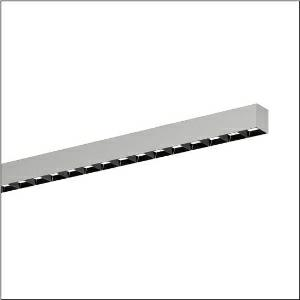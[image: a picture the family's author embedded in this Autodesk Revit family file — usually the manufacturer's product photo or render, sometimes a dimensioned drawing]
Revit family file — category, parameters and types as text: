
# Revit family: silica_21_51mx22tat4s
name_source: partatom
category: Lighting Fixtures
units: mm (PartAtom-declared; Revit-internal decimal feet)

## family parameters
Cut with Voids When Loaded = No
Host = Face
Light Source = No
Part Type = Normal
Room Calculation Point = No
Round Connector Dimension = Use Diameter
Shared = No

## types (1)
- --- (1 x LED, 3720 lm, 32.1 W, 6500K)
    Apparent Load = 32 VA
    CIE Flux Codes = 84 100 100 100 100
    Color Rendering = 80
    Color Temperature = 6500K
    Default Elevation = 1800 mm
    Description = Silica 21, office luminaire, primary light control with darklight reflector, of PMMA, black, CAT 2 (L<= 3000cd/m²), light emission: direct distribution, primary light characteristic: symmetric, installation type: surface-mounted, LED, rated luminous flux: 3.720lm, luminous efficacy: 110lm/W, light colour: 8tw, colour temperature: 2700..6500K, control gear: DALI DT8, with terminal, 3+2-pole, max. 2.5mm², mains connection: 220..240V, AC, 50/60Hz, rated input power: 33.8W, luminaire housing, of aluminium, metallic grey (RAL 9006), length: 1.204mm, width: 53mm, height: 53mm, protection rating (complete): IP20, insulation class (complete): insulation class I (protective earthing), certification: CE, permissible operating ambient temperature: 0..+35°C, standard: EN 50419, packaging unit: 1 piece
    Height = 53 mm
    Lamp = 1 x LED
    Lamp Light Flux = 3720 lm
    Lamp Power = 32.1 W
    Lamp count = 1
    Length = 1204 mm
    Luminous efficacy = 116 lm/W
    Manufacturer = Siteco
    ModVariant = No
    Model = 51MX22TAT4S
    Mounting Place = Ceiling
    Mounting Type = Surface mounted
    Number of Poles = 1
    OnlyDefault = Yes
    Power Factor = 1
    Product Name = Silica 21
    Product group = office luminaire | ceiling mounted
    ProductGroupID = 301
    Protection Class = Protection class I
    Protection Degree = IP 20
    RLX_Detail_Level = 1
    RLX_Emergency_Light_Flux = 0 lm
    RLX_Emergency_Type = 0
    RLX_Emergency_Type_DB = No
    RlxData = <blob elided: 39129 chars, md5=6030dded>
    Socket = socket
    Standby Power = 0 W
    System Light Flux = 3720 lm
    System Power = 32 W
    Type Comments = individual setting
    Type Image = l_1335929.jpg
    URL = http://relux.com
    VarID = @adj_139619
    Voltage = 0 V
    Weight = 0.00 kg
    Width = 53 mm

## geometry (parser evidence)
native form markers: Blend x4, Sweep x9
no freeform markers — native parametric forms only
